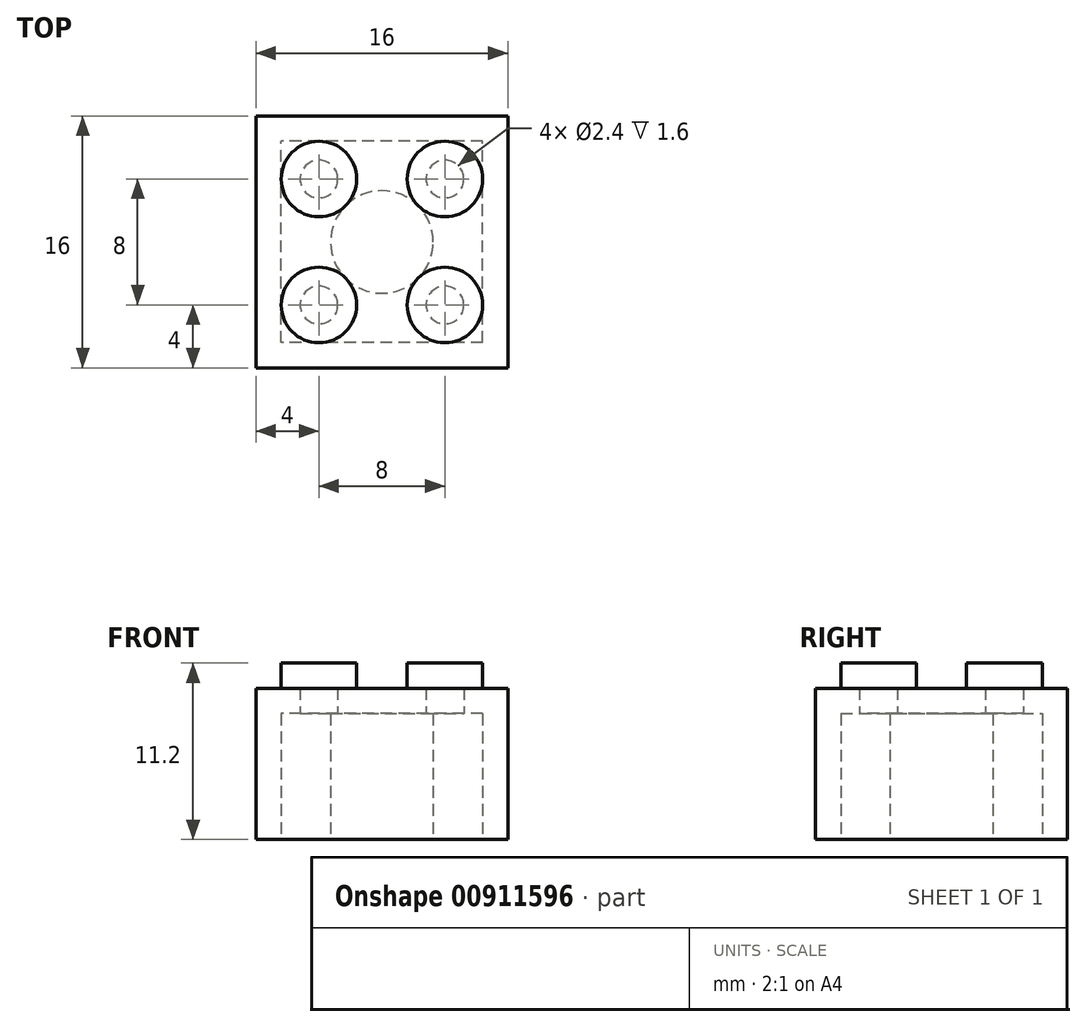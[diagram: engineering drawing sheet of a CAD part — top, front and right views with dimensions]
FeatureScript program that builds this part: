
annotation { "Feature Type Name" : "Feature", "Feature Type Description" : "" }
export const myFeature = defineFeature(function(context is Context, id is Id, definition is map)
    precondition{}
    {
        {
            var Q0;
            Q0=qCreatedBy(makeId("Top.planeOp"),FACE);
            var sketch = newSketch(context, id + "F0", { "sketchPlane" : qUnion([Q0])});
            skPoint(sketch, "E0.middle", {"position": v(-0.04, -0.04) * mm});
            skLineSegment(sketch, "E1.bottom", {"start": v(8, 8) * mm, "end": v(-8, 8) * mm});
            skLineSegment(sketch, "E1.top", {"start": v(8, -8) * mm, "end": v(-8, -8) * mm});
            skLineSegment(sketch, "E1.left", {"start": v(8, 8) * mm, "end": v(8, -8) * mm});
            skLineSegment(sketch, "E1.right", {"start": v(-8, 8) * mm, "end": v(-8, -8) * mm});
            skPoint(sketch, "E1.middle", {"position": v(0, 0) * mm});
            skSolve(sketch);
        }
        {
            var Q0;
            Q0=makeQuery(id+"F0.imprint","IMPRINT",FACE,{"disambiguationData":[TD([[makeQuery(id+"F0.imprint","IMPRINT",EDGE,{"derivedFrom":sQuery(id+"F0.wireOp",EDGE,"E1.bottom")}),1.0]])]});
            extrude(context, id + "F1", {"entities" : qUnion([Q0]), "depth" : 9.6 * mm, "offsetDistance" : 25 * mm});
        }
        {
            var Q0;
            Q0=makeQuery(id+"F1.opExtrude","CAP_FACE",FACE,{"disambiguationData":[OSD([sQuery(id+"F0.wireOp",EDGE,"E1.bottom"),sQuery(id+"F0.wireOp",EDGE,"E1.top"),sQuery(id+"F0.wireOp",EDGE,"E1.left"),sQuery(id+"F0.wireOp",EDGE,"E1.right")])],"isStart":true});
            var sketch = newSketch(context, id + "F2", { "sketchPlane" : qUnion([Q0])});
            skLineSegment(sketch, "E2.bottom", {"start": v(6.4, 6.4) * mm, "end": v(-6.4, 6.4) * mm});
            skLineSegment(sketch, "E2.top", {"start": v(6.4, -6.4) * mm, "end": v(-6.4, -6.4) * mm});
            skLineSegment(sketch, "E2.left", {"start": v(6.4, 6.4) * mm, "end": v(6.4, -6.4) * mm});
            skLineSegment(sketch, "E2.right", {"start": v(-6.4, 6.4) * mm, "end": v(-6.4, -6.4) * mm});
            skPoint(sketch, "E2.middle", {"position": v(0, 0) * mm});
            skCircle(sketch, "E3", {"center": v(0, 0) * mm, "radius": 3.26 * mm});
            skSolve(sketch);
        }
        {
            var Q0;
            Q0=makeQuery(id+"F2.imprint","IMPRINT",FACE,{"disambiguationData":[TD([[makeQuery(id+"F2.imprint","IMPRINT",EDGE,{"derivedFrom":sQuery(id+"F2.wireOp",EDGE,"E2.bottom")}),1.0]])]});
            extrude(context, id + "F3", {"entities" : qUnion([Q0]), "operationType" : NewBodyOperationType.REMOVE, "oppositeDirection" : true, "depth" : 8 * mm, "offsetDistance" : 25 * mm});
        }
        {
            var Q0;
            Q0=makeQuery(id+"F1.opExtrude","CAP_FACE",FACE,{"disambiguationData":[OSD([sQuery(id+"F0.wireOp",EDGE,"E1.bottom"),sQuery(id+"F0.wireOp",EDGE,"E1.top"),sQuery(id+"F0.wireOp",EDGE,"E1.left"),sQuery(id+"F0.wireOp",EDGE,"E1.right")])],"isStart":false});
            var sketch = newSketch(context, id + "F4", { "sketchPlane" : qUnion([Q0])});
            skCircle(sketch, "E4", {"center": v(4, 4) * mm, "radius": 2.4 * mm});
            skCircle(sketch, "E5", {"center": v(-4, 4) * mm, "radius": 2.4 * mm});
            skCircle(sketch, "E6", {"center": v(-4, -4) * mm, "radius": 2.4 * mm});
            skCircle(sketch, "E7", {"center": v(4, -4) * mm, "radius": 2.4 * mm});
            skSolve(sketch);
        }
        {
            var Q0;
            Q0=makeQuery(id+"F4.imprint","IMPRINT",FACE,{"disambiguationData":[TD([[makeQuery(id+"F4.imprint","IMPRINT",EDGE,{"derivedFrom":sQuery(id+"F4.wireOp",EDGE,"E5")}),1.0]])]});
            var Q1;
            Q1=makeQuery(id+"F4.imprint","IMPRINT",FACE,{"disambiguationData":[TD([[makeQuery(id+"F4.imprint","IMPRINT",EDGE,{"derivedFrom":sQuery(id+"F4.wireOp",EDGE,"E4")}),1.0]])]});
            var Q2;
            Q2=makeQuery(id+"F4.imprint","IMPRINT",FACE,{"disambiguationData":[TD([[makeQuery(id+"F4.imprint","IMPRINT",EDGE,{"derivedFrom":sQuery(id+"F4.wireOp",EDGE,"E6")}),1.0]])]});
            var Q3;
            Q3=makeQuery(id+"F4.imprint","IMPRINT",FACE,{"disambiguationData":[TD([[makeQuery(id+"F4.imprint","IMPRINT",EDGE,{"derivedFrom":sQuery(id+"F4.wireOp",EDGE,"E7")}),1.0]])]});
            extrude(context, id + "F5", {"entities" : qUnion([Q0, Q1, Q2, Q3]), "operationType" : NewBodyOperationType.ADD, "depth" : 1.6 * mm, "offsetDistance" : 25 * mm});
        }
        {
            var Q0;
            Q0=makeQuery(id+"F3.boolean.opBoolean","COPY",FACE,{"derivedFrom":makeQuery(id+"F3.opExtrude","CAP_FACE",FACE,{"disambiguationData":[OSD([sQuery(id+"F2.wireOp",EDGE,"E2.bottom"),sQuery(id+"F2.wireOp",EDGE,"E2.top"),sQuery(id+"F2.wireOp",EDGE,"E2.left"),sQuery(id+"F2.wireOp",EDGE,"E2.right"),sQuery(id+"F2.wireOp",EDGE,"E3")])],"isStart":false})});
            var sketch = newSketch(context, id + "F6", { "sketchPlane" : qUnion([Q0])});
            skCircle(sketch, "E8", {"center": v(4, 4) * mm, "radius": 1.2 * mm});
            skCircle(sketch, "E9", {"center": v(-4, 4) * mm, "radius": 1.2 * mm});
            skCircle(sketch, "E10", {"center": v(-4, -4) * mm, "radius": 1.2 * mm});
            skCircle(sketch, "E11", {"center": v(4, -4) * mm, "radius": 1.2 * mm});
            skSolve(sketch);
        }
        {
            var Q0;
            Q0=makeQuery(id+"F6.imprint","IMPRINT",FACE,{"disambiguationData":[TD([[makeQuery(id+"F6.imprint","IMPRINT",EDGE,{"derivedFrom":sQuery(id+"F6.wireOp",EDGE,"E10")}),1.0]])]});
            var Q1;
            Q1=makeQuery(id+"F6.imprint","IMPRINT",FACE,{"disambiguationData":[TD([[makeQuery(id+"F6.imprint","IMPRINT",EDGE,{"derivedFrom":sQuery(id+"F6.wireOp",EDGE,"E11")}),1.0]])]});
            var Q2;
            Q2=makeQuery(id+"F6.imprint","IMPRINT",FACE,{"disambiguationData":[TD([[makeQuery(id+"F6.imprint","IMPRINT",EDGE,{"derivedFrom":sQuery(id+"F6.wireOp",EDGE,"E9")}),1.0]])]});
            var Q3;
            Q3=makeQuery(id+"F6.imprint","IMPRINT",FACE,{"disambiguationData":[TD([[makeQuery(id+"F6.imprint","IMPRINT",EDGE,{"derivedFrom":sQuery(id+"F6.wireOp",EDGE,"E8")}),1.0]])]});
            extrude(context, id + "F7", {"entities" : qUnion([Q0, Q1, Q2, Q3]), "operationType" : NewBodyOperationType.REMOVE, "oppositeDirection" : true, "depth" : 1.6 * mm, "offsetDistance" : 25 * mm});
        }
    });
